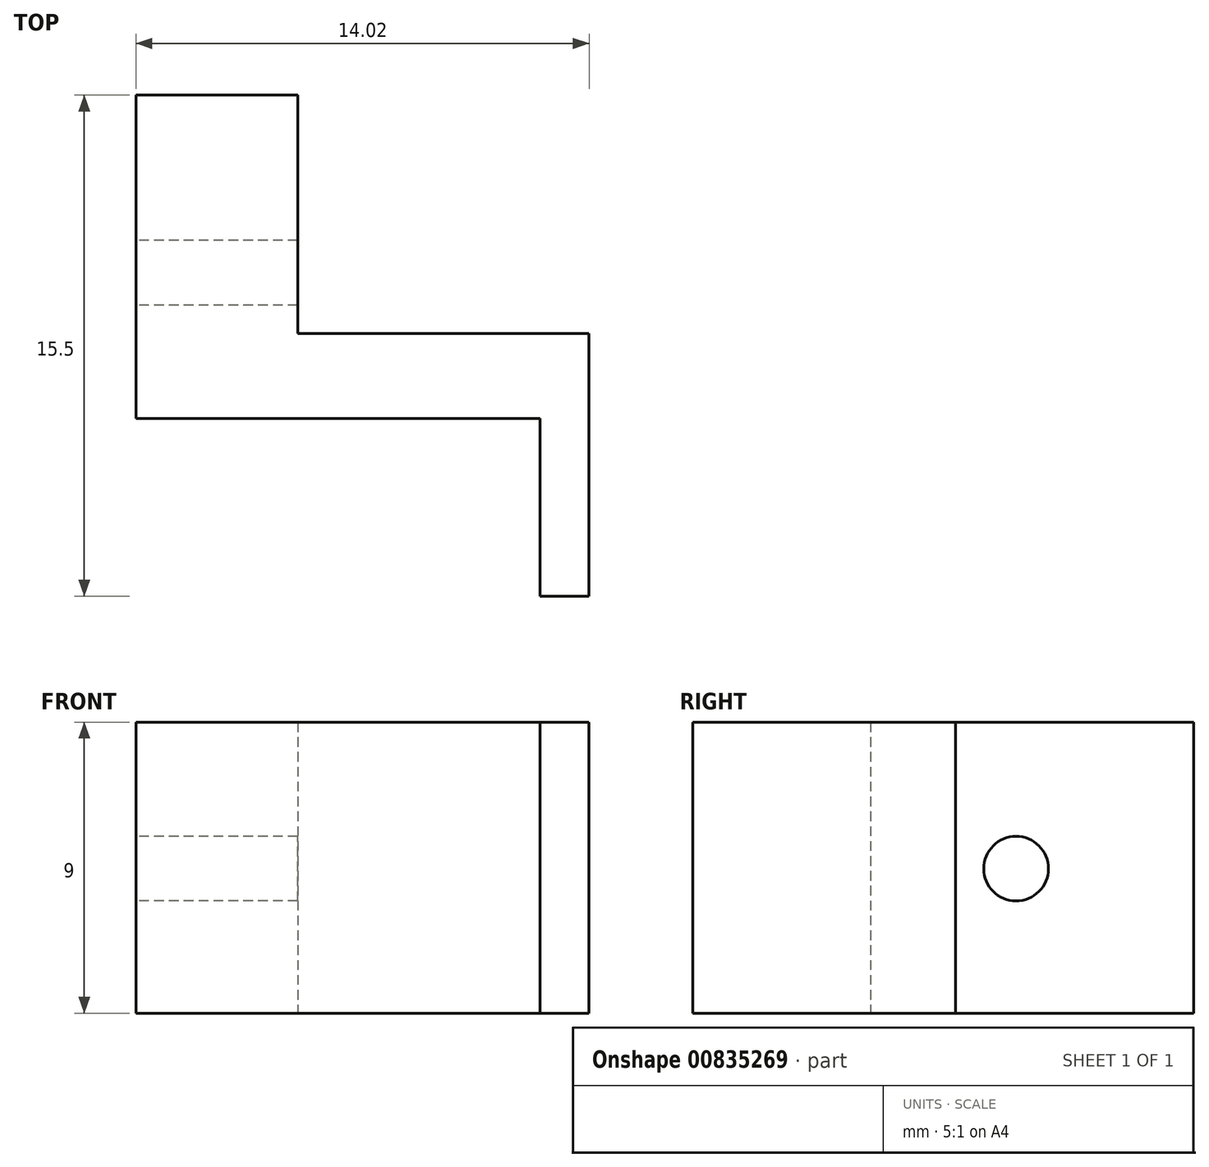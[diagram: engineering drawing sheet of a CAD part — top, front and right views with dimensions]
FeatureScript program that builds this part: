
annotation { "Feature Type Name" : "Feature", "Feature Type Description" : "" }
export const myFeature = defineFeature(function(context is Context, id is Id, definition is map)
    precondition{}
    {
        {
            var Q0;
            Q0=qCreatedBy(makeId("Top.planeOp"),FACE);
            var sketch = newSketch(context, id + "F0", { "sketchPlane" : qUnion([Q0])});
            skLineSegment(sketch, "E0", {"start": v(0, 7.37) * mm, "end": v(5, 7.37) * mm});
            skLineSegment(sketch, "E1", {"start": v(5, 7.37) * mm, "end": v(5, 0) * mm});
            skLineSegment(sketch, "E2", {"start": v(0, -2.63) * mm, "end": v(12.5, -2.63) * mm});
            skLineSegment(sketch, "E3", {"start": v(14.02, -2.63) * mm, "end": v(14.02, 0) * mm});
            skLineSegment(sketch, "E4", {"start": v(14.02, 0) * mm, "end": v(5, 0) * mm});
            skLineSegment(sketch, "E5", {"start": v(14.02, -2.63) * mm, "end": v(14.02, -8.13) * mm});
            skLineSegment(sketch, "E6", {"start": v(14.02, -8.13) * mm, "end": v(12.5, -8.13) * mm});
            skLineSegment(sketch, "E7", {"start": v(12.5, -8.13) * mm, "end": v(12.5, -2.63) * mm});
            skLineSegment(sketch, "E8", {"start": v(0, 7.37) * mm, "end": v(0, -2.63) * mm});
            skSolve(sketch);
        }
        {
            var Q0;
            Q0 = qSketchRegion(id + "F0", true);
            extrude(context, id + "F1", {"entities" : qUnion([Q0]), "depth" : 9 * mm, "offsetDistance" : 25 * mm});
        }
        {
            var Q0;
            Q0=makeQuery(id+"F1.opExtrude","SWEPT_FACE",FACE,{"disambiguationData":[OSD([sQuery(id+"F0.wireOp",EDGE,"E8")])]});
            var sketch = newSketch(context, id + "F2", { "sketchPlane" : qUnion([Q0])});
            skCircle(sketch, "E9", {"center": v(-1.87, 4.47) * mm, "radius": 1 * mm});
            skSolve(sketch);
        }
        {
            var Q0;
            Q0 = qSketchRegion(id + "F2", true);
            extrude(context, id + "F3", {"entities" : qUnion([Q0]), "operationType" : NewBodyOperationType.REMOVE, "oppositeDirection" : true, "depth" : 25 * mm, "offsetDistance" : 25 * mm});
        }
    });
